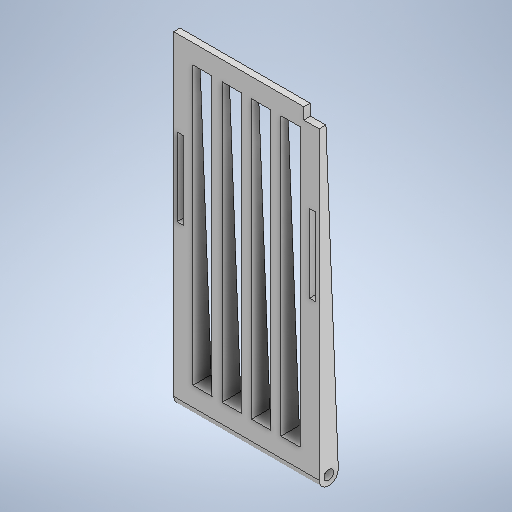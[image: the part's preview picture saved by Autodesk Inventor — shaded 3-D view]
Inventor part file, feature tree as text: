
AUTODESK INVENTOR PART (.ipt)
format: ipt  version: 2025.1 (Build 291241020, 241B)  size: 341,504 bytes
history: native  units: mm
features: extrude x7, sketch x7, plane x2, fillet x1, pattern_linear x1, mirror x1
ambient origin geometry x8: Origin, YZ Plane, XZ Plane, XY Plane, X Axis, Y Axis, Z Axis, Center Point
bodies: Solid1 (feature_tree)
feature tree (19):
  extrude  "Extrusion1"  Depth=170.0mm
  fillet  "Fillet1"  Radius=10.0mm
  extrude  "Extrusion3"  Depth=5.0mm
  extrude  "Extrusion4"  TaperAngle=0.0deg  [1 undecoded]
  pattern_linear  "Rectangular Pattern1"  Count1=16  [1 undecoded]
  extrude  "Extrusion5"  TaperAngle=0.0deg  [1 undecoded]
  extrude  "Extrusion7"  Depth=3.0mm
  plane  "Work Plane1"
  plane  "Work Plane2"
  mirror  "Mirror2"
  extrude  "Extrusion8"  Depth=2.5mm
  extrude  "Extrusion9"  TaperAngle=0.0deg  [1 undecoded]
  sketch  "Sketch1"  dims[d0=76.0mm d2=170.0mm d4=10.0mm d5=0.0mm]
  sketch  "Sketch4"  dims[d18=5.0mm d22=171.925mm]
  sketch  "Sketch5"  dims[d23=7.0mm d24=0.0mm d25=0.0mm]
  sketch  "Sketch6"  dims[d26=15.0mm]
  sketch  "Sketch8"  dims[d27=10.0mm d28=160.0mm]
  sketch  "Sketch9"  dims[d29=10.0mm d30=0.0mm d31=0.0mm]
  sketch  "Sketch10"  dims[d32=40.0mm d34=15.3333mm d36=3.0mm d37=2.5mm d38=0.0mm d39=0.0mm d43=3.3mm d45=79.9mm d47=0.0mm d48=0.0mm d49=1.75mm d50=8.0mm d51=6.0mm d52=0.0mm d53=0.0mm d55=4.0mm d56=0.0mm d58=5.0mm d59=40.6mm]
note: 4 required parameter values undecoded (feature->parameter linkage not recoverable at this tier; creation-order binding heuristic only, values carry confidence <= 0.55)
